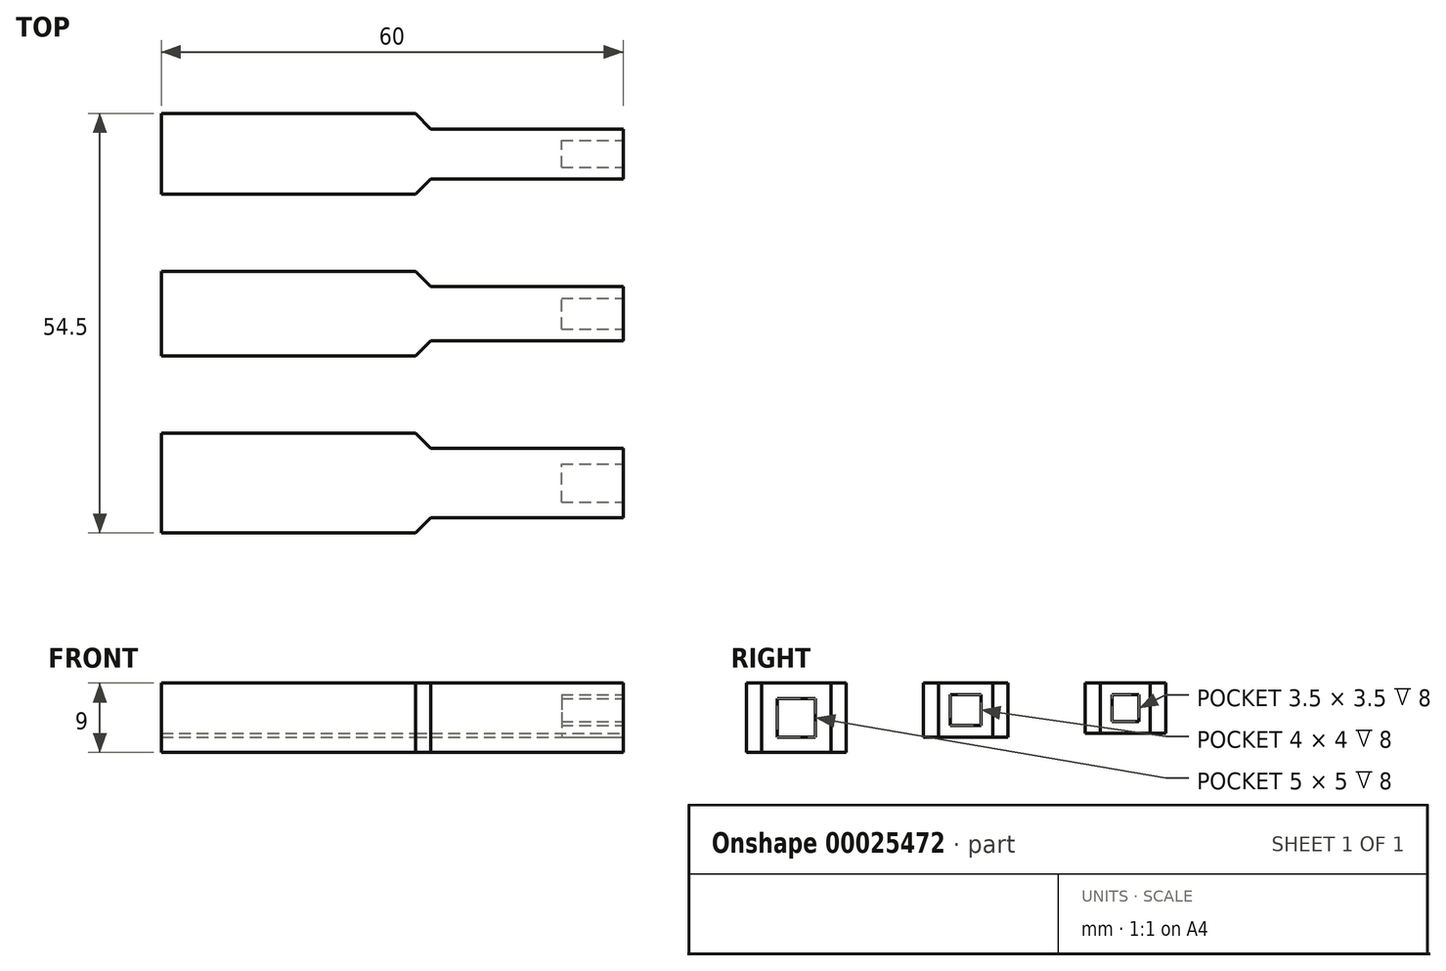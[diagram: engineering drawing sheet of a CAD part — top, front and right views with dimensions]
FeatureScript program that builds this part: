
annotation { "Feature Type Name" : "Feature", "Feature Type Description" : "" }
export const myFeature = defineFeature(function(context is Context, id is Id, definition is map)
    precondition{}
    {
        {
            var Q0;
            Q0=qCreatedBy(makeId("Right.planeOp"),FACE);
            var sketch = newSketch(context, id + "F0", { "sketchPlane" : qUnion([Q0])});
            skLineSegment(sketch, "E0.bottom", {"start": v(30.02, 6.08) * mm, "end": v(33.52, 6.08) * mm});
            skLineSegment(sketch, "E0.top", {"start": v(30.02, 2.58) * mm, "end": v(33.52, 2.58) * mm});
            skLineSegment(sketch, "E0.left", {"start": v(30.02, 6.08) * mm, "end": v(30.02, 2.58) * mm});
            skLineSegment(sketch, "E0.right", {"start": v(33.52, 6.08) * mm, "end": v(33.52, 2.58) * mm});
            skLineSegment(sketch, "E1.0", {"start": v(28.52, 7.58) * mm, "end": v(35.02, 7.58) * mm});
            skLineSegment(sketch, "E1.1", {"start": v(28.52, 7.58) * mm, "end": v(28.52, 1.08) * mm});
            skLineSegment(sketch, "E1.2", {"start": v(28.52, 1.08) * mm, "end": v(35.02, 1.08) * mm});
            skLineSegment(sketch, "E1.3", {"start": v(35.02, 7.58) * mm, "end": v(35.02, 1.08) * mm});
            skLineSegment(sketch, "E2.bottom", {"start": v(26.52, 7.58) * mm, "end": v(37.02, 7.58) * mm});
            skLineSegment(sketch, "E2.top", {"start": v(26.52, 1.08) * mm, "end": v(37.02, 1.08) * mm});
            skLineSegment(sketch, "E2.left", {"start": v(26.52, 7.58) * mm, "end": v(26.52, 1.08) * mm});
            skLineSegment(sketch, "E2.right", {"start": v(37.02, 7.58) * mm, "end": v(37.02, 1.08) * mm});
            skSolve(sketch);
        }
        {
            var Q0;
            Q0=qCreatedBy(makeId("Right.planeOp"),FACE);
            var sketch = newSketch(context, id + "F1", { "sketchPlane" : qUnion([Q0])});
            skLineSegment(sketch, "E3.bottom", {"start": v(9.02, 6.08) * mm, "end": v(13.02, 6.08) * mm});
            skLineSegment(sketch, "E3.top", {"start": v(9.02, 2.08) * mm, "end": v(13.02, 2.08) * mm});
            skLineSegment(sketch, "E3.left", {"start": v(9.02, 6.08) * mm, "end": v(9.02, 2.08) * mm});
            skLineSegment(sketch, "E3.right", {"start": v(13.02, 6.08) * mm, "end": v(13.02, 2.08) * mm});
            skLineSegment(sketch, "E4.0", {"start": v(7.52, 7.58) * mm, "end": v(14.52, 7.58) * mm});
            skLineSegment(sketch, "E4.1", {"start": v(7.52, 7.58) * mm, "end": v(7.52, 0.58) * mm});
            skLineSegment(sketch, "E4.2", {"start": v(7.52, 0.58) * mm, "end": v(14.52, 0.58) * mm});
            skLineSegment(sketch, "E4.3", {"start": v(14.52, 7.58) * mm, "end": v(14.52, 0.58) * mm});
            skLineSegment(sketch, "E5.bottom", {"start": v(5.52, 7.58) * mm, "end": v(16.52, 7.58) * mm});
            skLineSegment(sketch, "E5.top", {"start": v(5.52, 0.58) * mm, "end": v(16.52, 0.58) * mm});
            skLineSegment(sketch, "E5.left", {"start": v(5.52, 7.58) * mm, "end": v(5.52, 0.58) * mm});
            skLineSegment(sketch, "E5.right", {"start": v(16.52, 7.58) * mm, "end": v(16.52, 0.58) * mm});
            skSolve(sketch);
        }
        {
            var Q0;
            Q0=qCreatedBy(makeId("Right.planeOp"),FACE);
            var sketch = newSketch(context, id + "F2", { "sketchPlane" : qUnion([Q0])});
            skLineSegment(sketch, "E6.bottom", {"start": v(-13.48, 5.58) * mm, "end": v(-8.48, 5.58) * mm});
            skLineSegment(sketch, "E6.top", {"start": v(-13.48, 0.58) * mm, "end": v(-8.48, 0.58) * mm});
            skLineSegment(sketch, "E6.left", {"start": v(-13.48, 5.58) * mm, "end": v(-13.48, 0.58) * mm});
            skLineSegment(sketch, "E6.right", {"start": v(-8.48, 5.58) * mm, "end": v(-8.48, 0.58) * mm});
            skLineSegment(sketch, "E7.0", {"start": v(-15.48, 7.58) * mm, "end": v(-6.48, 7.58) * mm});
            skLineSegment(sketch, "E7.1", {"start": v(-15.48, 7.58) * mm, "end": v(-15.48, -1.42) * mm});
            skLineSegment(sketch, "E7.2", {"start": v(-15.48, -1.42) * mm, "end": v(-6.48, -1.42) * mm});
            skLineSegment(sketch, "E7.3", {"start": v(-6.48, 7.58) * mm, "end": v(-6.48, -1.42) * mm});
            skLineSegment(sketch, "E8.bottom", {"start": v(-17.48, 7.58) * mm, "end": v(-4.48, 7.58) * mm});
            skLineSegment(sketch, "E8.top", {"start": v(-17.48, -1.42) * mm, "end": v(-4.48, -1.42) * mm});
            skLineSegment(sketch, "E8.left", {"start": v(-17.48, 7.58) * mm, "end": v(-17.48, -1.42) * mm});
            skLineSegment(sketch, "E8.right", {"start": v(-4.48, 7.58) * mm, "end": v(-4.48, -1.42) * mm});
            skSolve(sketch);
        }
        {
            var Q0;
            Q0=makeQuery(id+"F0.imprint","IMPRINT",FACE,{"disambiguationData":[TD([[makeQuery(id+"F0.imprint","IMPRINT",EDGE,{"derivedFrom":sQuery(id+"F0.wireOp",EDGE,"E0.bottom")}),1.0]])]});
            var Q1;
            Q1=makeQuery(id+"F0.imprint","IMPRINT",FACE,{"disambiguationData":[TD([[makeQuery(id+"F0.imprint","IMPRINT",EDGE,{"derivedFrom":sQuery(id+"F0.wireOp",EDGE,"E0.bottom")}),-1.0]])]});
            var Q2;
            {var subQ2=sQuery(id+"F0.wireOp",EDGE,"E1.1");Q2=makeQuery(id+"F0.imprint","IMPRINT",FACE,{"disambiguationData":[TD([[makeQuery(id+"F0.imprint","IMPRINT",EDGE,{"derivedFrom":subQ2}),-1.0]])]});}
            var Q3;
            {var subQ2=sQuery(id+"F0.wireOp",EDGE,"E1.3");Q3=makeQuery(id+"F0.imprint","IMPRINT",FACE,{"disambiguationData":[TD([[makeQuery(id+"F0.imprint","IMPRINT",EDGE,{"derivedFrom":subQ2}),1.0]])]});}
            var Q4;
            {var subQ2=sQuery(id+"F1.wireOp",EDGE,"E4.1");Q4=makeQuery(id+"F1.imprint","IMPRINT",FACE,{"disambiguationData":[TD([[makeQuery(id+"F1.imprint","IMPRINT",EDGE,{"derivedFrom":subQ2}),-1.0]])]});}
            var Q5;
            Q5=makeQuery(id+"F1.imprint","IMPRINT",FACE,{"disambiguationData":[TD([[makeQuery(id+"F1.imprint","IMPRINT",EDGE,{"derivedFrom":sQuery(id+"F1.wireOp",EDGE,"E3.bottom")}),1.0]])]});
            var Q6;
            {var subQ2=sQuery(id+"F1.wireOp",EDGE,"E4.3");Q6=makeQuery(id+"F1.imprint","IMPRINT",FACE,{"disambiguationData":[TD([[makeQuery(id+"F1.imprint","IMPRINT",EDGE,{"derivedFrom":subQ2}),1.0]])]});}
            var Q7;
            Q7=makeQuery(id+"F1.imprint","IMPRINT",FACE,{"disambiguationData":[TD([[makeQuery(id+"F1.imprint","IMPRINT",EDGE,{"derivedFrom":sQuery(id+"F1.wireOp",EDGE,"E3.bottom")}),-1.0]])]});
            var Q8;
            {var subQ2=sQuery(id+"F2.wireOp",EDGE,"E7.1");Q8=makeQuery(id+"F2.imprint","IMPRINT",FACE,{"disambiguationData":[TD([[makeQuery(id+"F2.imprint","IMPRINT",EDGE,{"derivedFrom":subQ2}),-1.0]])]});}
            var Q9;
            Q9=makeQuery(id+"F2.imprint","IMPRINT",FACE,{"disambiguationData":[TD([[makeQuery(id+"F2.imprint","IMPRINT",EDGE,{"derivedFrom":sQuery(id+"F2.wireOp",EDGE,"E6.bottom")}),1.0]])]});
            var Q10;
            Q10=makeQuery(id+"F2.imprint","IMPRINT",FACE,{"disambiguationData":[TD([[makeQuery(id+"F2.imprint","IMPRINT",EDGE,{"derivedFrom":sQuery(id+"F2.wireOp",EDGE,"E6.bottom")}),-1.0]])]});
            var Q11;
            {var subQ2=sQuery(id+"F2.wireOp",EDGE,"E7.3");Q11=makeQuery(id+"F2.imprint","IMPRINT",FACE,{"disambiguationData":[TD([[makeQuery(id+"F2.imprint","IMPRINT",EDGE,{"derivedFrom":subQ2}),1.0]])]});}
            extrude(context, id + "F3", {"entities" : qUnion([Q0, Q1, Q2, Q3, Q4, Q5, Q6, Q7, Q8, Q9, Q10, Q11]), "oppositeDirection" : true, "depth" : 60 * mm});
        }
        {
            var Q0;
            Q0=makeQuery(id+"F0.imprint","IMPRINT",FACE,{"disambiguationData":[TD([[makeQuery(id+"F0.imprint","IMPRINT",EDGE,{"derivedFrom":sQuery(id+"F0.wireOp",EDGE,"E0.bottom")}),-1.0]])]});
            var Q1;
            Q1=makeQuery(id+"F1.imprint","IMPRINT",FACE,{"disambiguationData":[TD([[makeQuery(id+"F1.imprint","IMPRINT",EDGE,{"derivedFrom":sQuery(id+"F1.wireOp",EDGE,"E3.bottom")}),-1.0]])]});
            var Q2;
            Q2=makeQuery(id+"F2.imprint","IMPRINT",FACE,{"disambiguationData":[TD([[makeQuery(id+"F2.imprint","IMPRINT",EDGE,{"derivedFrom":sQuery(id+"F2.wireOp",EDGE,"E6.bottom")}),-1.0]])]});
            extrude(context, id + "F4", {"entities" : qUnion([Q0, Q1, Q2]), "operationType" : NewBodyOperationType.REMOVE, "oppositeDirection" : true, "depth" : 8 * mm});
        }
        {
            var Q0;
            {var subQ2=sQuery(id+"F0.wireOp",EDGE,"E1.1");Q0=makeQuery(id+"F0.imprint","IMPRINT",FACE,{"disambiguationData":[TD([[makeQuery(id+"F0.imprint","IMPRINT",EDGE,{"derivedFrom":subQ2}),-1.0]])]});}
            var Q1;
            {var subQ2=sQuery(id+"F0.wireOp",EDGE,"E1.3");Q1=makeQuery(id+"F0.imprint","IMPRINT",FACE,{"disambiguationData":[TD([[makeQuery(id+"F0.imprint","IMPRINT",EDGE,{"derivedFrom":subQ2}),1.0]])]});}
            var Q2;
            {var subQ2=sQuery(id+"F1.wireOp",EDGE,"E4.1");Q2=makeQuery(id+"F1.imprint","IMPRINT",FACE,{"disambiguationData":[TD([[makeQuery(id+"F1.imprint","IMPRINT",EDGE,{"derivedFrom":subQ2}),-1.0]])]});}
            var Q3;
            {var subQ2=sQuery(id+"F1.wireOp",EDGE,"E4.3");Q3=makeQuery(id+"F1.imprint","IMPRINT",FACE,{"disambiguationData":[TD([[makeQuery(id+"F1.imprint","IMPRINT",EDGE,{"derivedFrom":subQ2}),1.0]])]});}
            var Q4;
            {var subQ2=sQuery(id+"F2.wireOp",EDGE,"E7.3");Q4=makeQuery(id+"F2.imprint","IMPRINT",FACE,{"disambiguationData":[TD([[makeQuery(id+"F2.imprint","IMPRINT",EDGE,{"derivedFrom":subQ2}),1.0]])]});}
            var Q5;
            {var subQ2=sQuery(id+"F2.wireOp",EDGE,"E7.1");Q5=makeQuery(id+"F2.imprint","IMPRINT",FACE,{"disambiguationData":[TD([[makeQuery(id+"F2.imprint","IMPRINT",EDGE,{"derivedFrom":subQ2}),-1.0]])]});}
            extrude(context, id + "F5", {"entities" : qUnion([Q0, Q1, Q2, Q3, Q4, Q5]), "operationType" : NewBodyOperationType.REMOVE, "oppositeDirection" : true, "depth" : 30 * mm});
        }
        {
            var Q0;
            Q0=makeQuery(id+"F5.boolean.opBoolean","COPY",EDGE,{"derivedFrom":makeQuery(id+"F5.opExtrude","CAP_EDGE",EDGE,{"disambiguationData":[OSD([sQuery(id+"F0.wireOp",EDGE,"E1.1")])],"isStart":false})});
            var Q1;
            Q1=makeQuery(id+"F5.boolean.opBoolean","COPY",EDGE,{"derivedFrom":makeQuery(id+"F5.opExtrude","CAP_EDGE",EDGE,{"disambiguationData":[OSD([sQuery(id+"F0.wireOp",EDGE,"E1.3")])],"isStart":false})});
            var Q2;
            Q2=makeQuery(id+"F5.boolean.opBoolean","COPY",EDGE,{"derivedFrom":makeQuery(id+"F5.opExtrude","CAP_EDGE",EDGE,{"disambiguationData":[OSD([sQuery(id+"F1.wireOp",EDGE,"E4.3")])],"isStart":false})});
            var Q3;
            Q3=makeQuery(id+"F5.boolean.opBoolean","COPY",EDGE,{"derivedFrom":makeQuery(id+"F5.opExtrude","CAP_EDGE",EDGE,{"disambiguationData":[OSD([sQuery(id+"F1.wireOp",EDGE,"E4.1")])],"isStart":false})});
            var Q4;
            Q4=makeQuery(id+"F5.boolean.opBoolean","COPY",EDGE,{"derivedFrom":makeQuery(id+"F5.opExtrude","CAP_EDGE",EDGE,{"disambiguationData":[OSD([sQuery(id+"F2.wireOp",EDGE,"E7.3")])],"isStart":false})});
            var Q5;
            Q5=makeQuery(id+"F5.boolean.opBoolean","COPY",EDGE,{"derivedFrom":makeQuery(id+"F5.opExtrude","CAP_EDGE",EDGE,{"disambiguationData":[OSD([sQuery(id+"F2.wireOp",EDGE,"E7.1")])],"isStart":false})});
            chamfer(context, id + "F6", {"entities" : qUnion([Q0, Q1, Q2, Q3, Q4, Q5]), "width" : 5 * mm, "tangentPropagation" : true});
        }
    });
